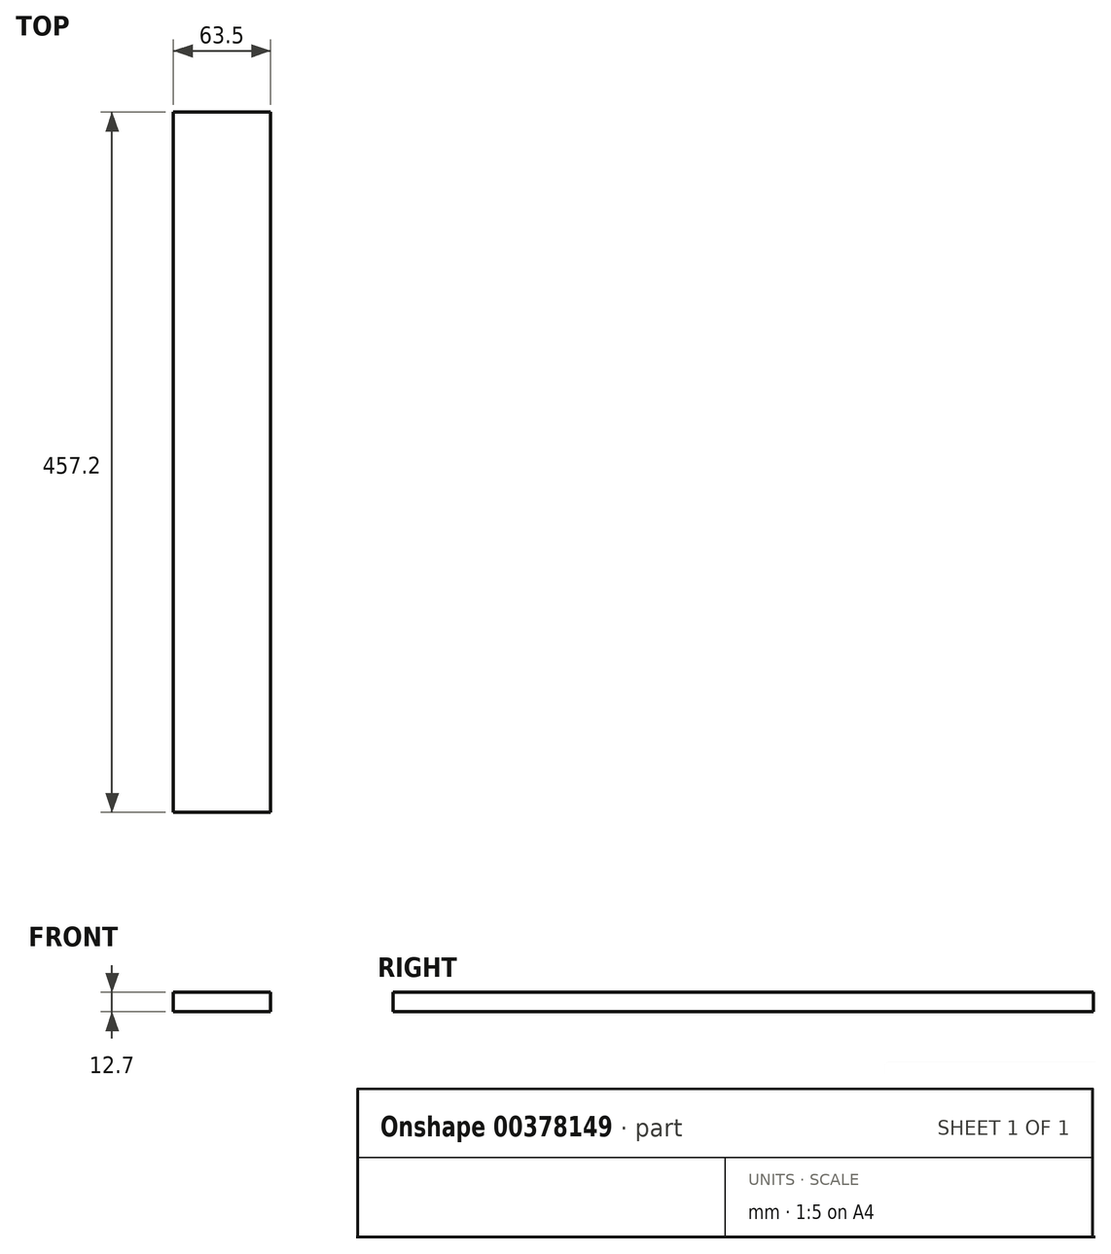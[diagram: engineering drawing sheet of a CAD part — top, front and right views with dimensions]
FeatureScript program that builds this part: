
annotation { "Feature Type Name" : "Feature", "Feature Type Description" : "" }
export const myFeature = defineFeature(function(context is Context, id is Id, definition is map)
    precondition{}
    {
        {
            var Q0;
            Q0=qCreatedBy(makeId("Front.planeOp"),FACE);
            var sketch = newSketch(context, id + "F0", { "sketchPlane" : qUnion([Q0])});
            skLineSegment(sketch, "E0.bottom", {"start": v(31.75, 6.35) * mm, "end": v(-31.75, 6.35) * mm});
            skLineSegment(sketch, "E0.top", {"start": v(31.75, -6.35) * mm, "end": v(-31.75, -6.35) * mm});
            skLineSegment(sketch, "E0.left", {"start": v(31.75, 6.35) * mm, "end": v(31.75, -6.35) * mm});
            skLineSegment(sketch, "E0.right", {"start": v(-31.75, 6.35) * mm, "end": v(-31.75, -6.35) * mm});
            skPoint(sketch, "E0.middle", {"position": v(0, 0) * mm});
            skSolve(sketch);
        }
        {
            var Q0;
            Q0=qSketchRegion(id+"F0",true);
            extrude(context, id + "F1", {"entities" : qUnion([Q0]), "endBound" : BoundingType.SYMMETRIC, "depth" : 457.2 * mm});
        }
    });
